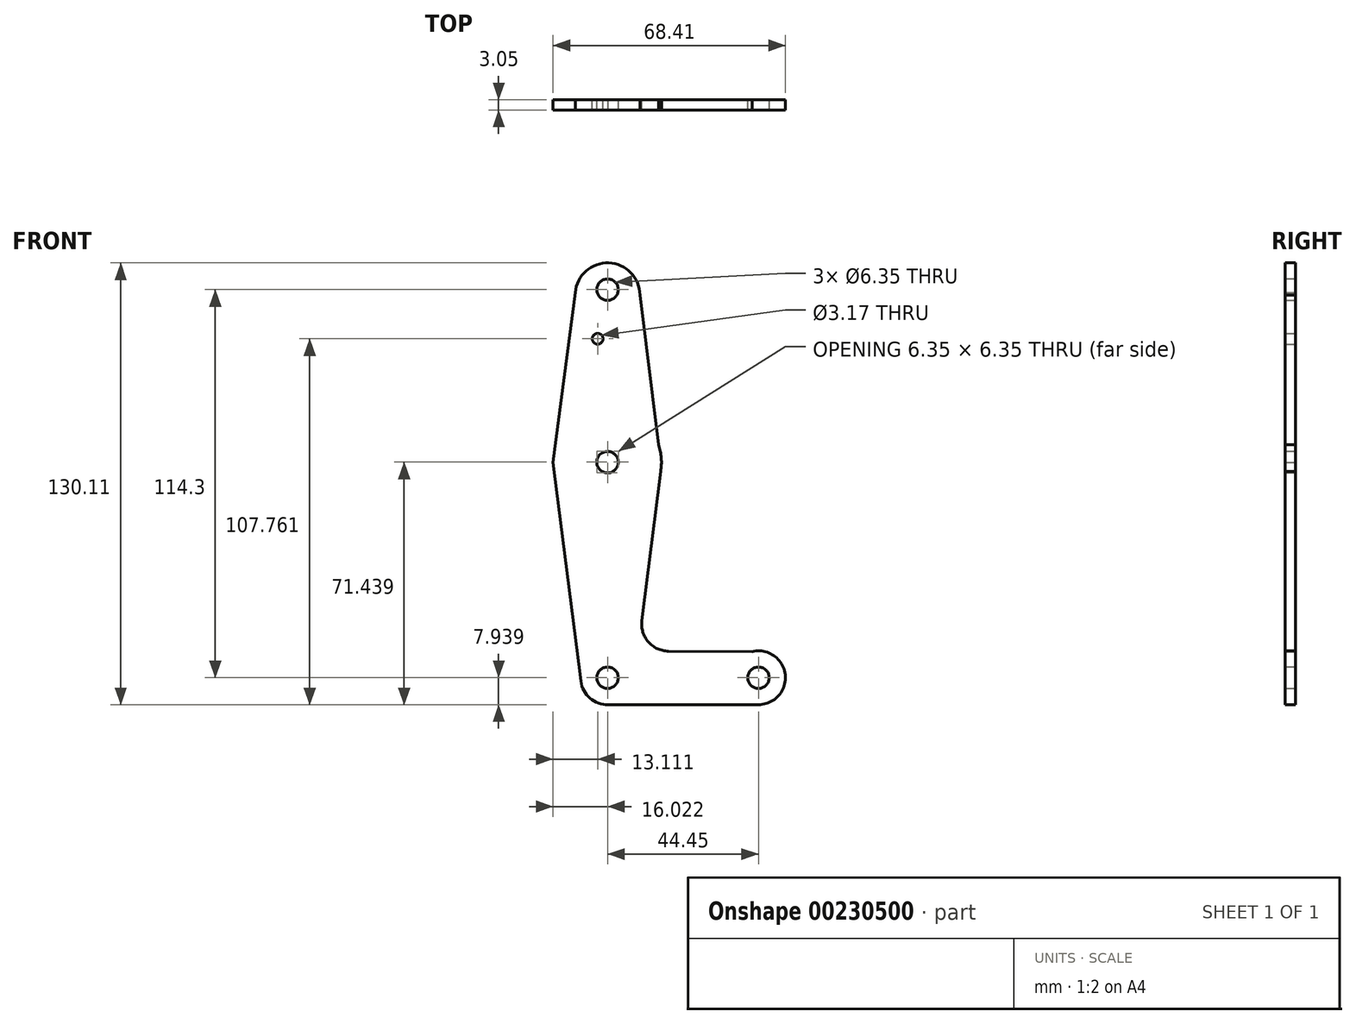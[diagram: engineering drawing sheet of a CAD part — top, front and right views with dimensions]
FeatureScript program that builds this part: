
annotation { "Feature Type Name" : "Feature", "Feature Type Description" : "" }
export const myFeature = defineFeature(function(context is Context, id is Id, definition is map)
    precondition{}
    {
        {
            var Q0;
            Q0=qCreatedBy(makeId("Front.planeOp"),FACE);
            var sketch = newSketch(context, id + "F0", { "sketchPlane" : qUnion([Q0])});
            skLineSegment(sketch, "E0", {"start": v(-61, -48.98) * mm, "end": v(-16.56, -48.98) * mm});
            skCircle(sketch, "E1", {"center": v(-61, 63.67) * mm, "radius": 9.53 * mm});
            skCircle(sketch, "E2", {"center": v(-61, 14.52) * mm, "radius": 15.88 * mm});
            skCircle(sketch, "E3", {"center": v(-61, -48.98) * mm, "radius": 7.94 * mm});
            skCircle(sketch, "E4", {"center": v(-16.56, -48.98) * mm, "radius": 7.94 * mm});
            skLineSegment(sketch, "E5", {"start": v(-61, 65.32) * mm, "end": v(-61, 63.67) * mm});
            skLineSegment(sketch, "E6", {"start": v(-61, 63.67) * mm, "end": v(-61, -48.98) * mm});
            skLineSegment(sketch, "E7", {"start": v(-70.5, 64.48) * mm, "end": v(-77.03, 14.46) * mm});
            skLineSegment(sketch, "E8", {"start": v(-77.03, 14.46) * mm, "end": v(-68.88, -49.98) * mm});
            skLineSegment(sketch, "E9", {"start": v(-51.48, 63.76) * mm, "end": v(-45.18, 13.3) * mm});
            skLineSegment(sketch, "E10", {"start": v(-45.18, 13.3) * mm, "end": v(-50.9, -32.2) * mm});
            skLineSegment(sketch, "E11", {"start": v(-60.76, -56.92) * mm, "end": v(-16.56, -56.92) * mm});
            skLineSegment(sketch, "E12", {"start": v(-43.05, -41.14) * mm, "end": v(-14.6, -41.29) * mm});
            skCircle(sketch, "E13", {"center": v(-61, 65.32) * mm, "radius": 3.18 * mm});
            skCircle(sketch, "E14", {"center": v(-61, 14.52) * mm, "radius": 3.18 * mm});
            skCircle(sketch, "E15", {"center": v(-61, -48.98) * mm, "radius": 3.18 * mm});
            skCircle(sketch, "E16", {"center": v(-16.56, -48.98) * mm, "radius": 3.18 * mm});
            skArc(sketch, "E17.filletArc", {"start": v(-50.9, -32.2) * mm, "mid": v(-48.99, -38.43) * mm, "end": v(-43.05, -41.14) * mm});
            skCircle(sketch, "E18", {"center": v(-63.92, 50.84) * mm, "radius": 1.59 * mm});
            skSolve(sketch);
        }
        {
            var Q0;
            Q0 = qSketchRegion(id + "F0", true);
            var Q1;
            {var subQ0=sQuery(id+"F0.wireOp",EDGE,"E15");var subQ1=sQuery(id+"F0.wireOp",EDGE,"E0");var subQ2=makeQuery(id+"F0.imprint","INTERSECT",VERTEX,{"derivedFrom":[subQ1,subQ0]});Q1=makeQuery(id+"F0.imprint","IMPRINT",FACE,{"disambiguationData":[TD([[makeQuery(id+"F0.imprint","IMPRINT",EDGE,{"disambiguationData":[TD([[subQ2,-1.0]])],"derivedFrom":subQ1}),1.0]])]});}
            extrude(context, id + "F1", {"entities" : qUnion([Q0, Q1]), "depth" : 3.05 * mm});
        }
    });
